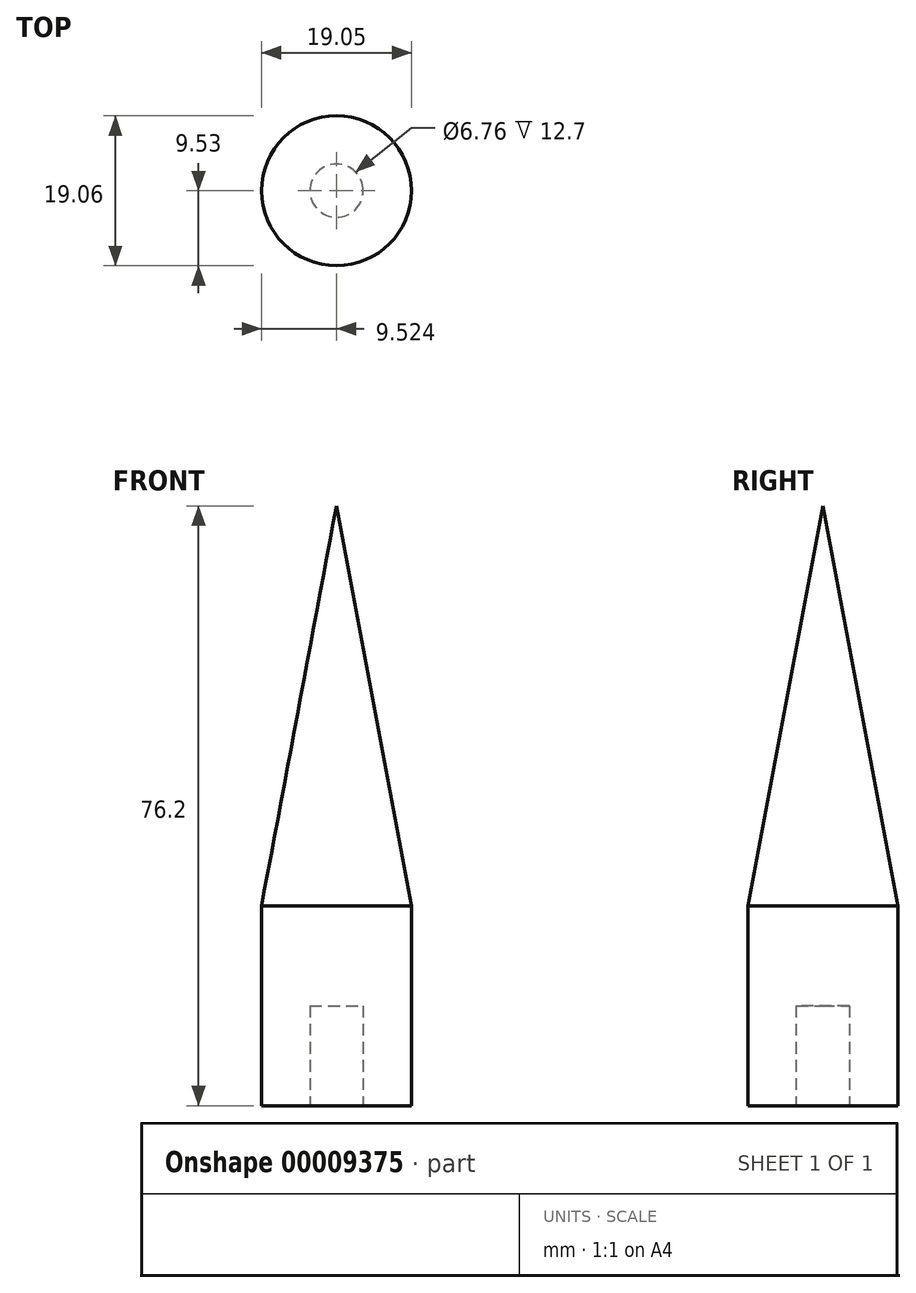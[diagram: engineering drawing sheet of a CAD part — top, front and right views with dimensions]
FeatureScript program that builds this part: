
annotation { "Feature Type Name" : "Feature", "Feature Type Description" : "" }
export const myFeature = defineFeature(function(context is Context, id is Id, definition is map)
    precondition{}
    {
        {
            var Q0;
            Q0=qCreatedBy(makeId("Front.planeOp"),FACE);
            var sketch = newSketch(context, id + "F0", { "sketchPlane" : qUnion([Q0])});
            skLineSegment(sketch, "E0", {"start": v(52.3, 0) * mm, "end": v(42.77, 50.8) * mm});
            skLineSegment(sketch, "E1", {"start": v(42.77, 50.8) * mm, "end": v(42.77, 0) * mm});
            skLineSegment(sketch, "E2", {"start": v(42.77, 0) * mm, "end": v(42.77, -25.4) * mm});
            skLineSegment(sketch, "E3", {"start": v(42.77, -25.4) * mm, "end": v(52.3, -25.4) * mm});
            skLineSegment(sketch, "E4", {"start": v(52.3, -25.4) * mm, "end": v(52.3, 0) * mm});
            skSolve(sketch);
        }
        {
            var Q0;
            Q0=makeQuery(id+"F0.imprint","IMPRINT",FACE,{"disambiguationData":[TD([[makeQuery(id+"F0.imprint","IMPRINT",EDGE,{"derivedFrom":sQuery(id+"F0.wireOp",EDGE,"E0")}),1.0]])]});
            var Q1;
            Q1=sQuery(id+"F0.wireOp",EDGE,"E1");
            revolve(context, id + "F1", {"entities" : qUnion([Q0]), "axis" : qUnion([Q1]), "revolveType" : RevolveType.FULL});
        }
        {
            var Q0;
            Q0=makeQuery(id+"F1.opRevolve","SWEPT_FACE",FACE,{"disambiguationData":[OSD([sQuery(id+"F0.wireOp",EDGE,"E3")])]});
            var sketch = newSketch(context, id + "F2", { "sketchPlane" : qUnion([Q0])});
            skCircle(sketch, "E5", {"center": v(42.77, 0) * mm, "radius": 3.38 * mm});
            skSolve(sketch);
        }
        {
            var Q0;
            Q0=makeQuery(id+"F2.imprint","IMPRINT",FACE,{"disambiguationData":[TD([[makeQuery(id+"F2.imprint","IMPRINT",EDGE,{"derivedFrom":sQuery(id+"F2.wireOp",EDGE,"E5")}),1.0]])]});
            extrude(context, id + "F3", {"entities" : qUnion([Q0]), "operationType" : NewBodyOperationType.REMOVE, "oppositeDirection" : true, "depth" : 12.7 * mm});
        }
    });
